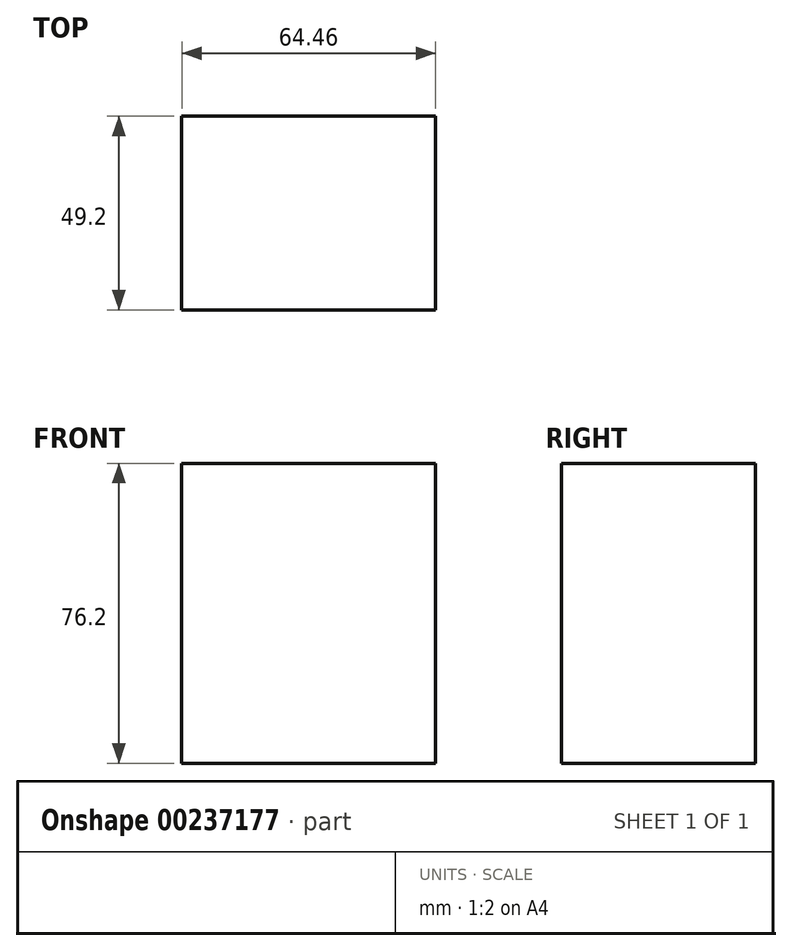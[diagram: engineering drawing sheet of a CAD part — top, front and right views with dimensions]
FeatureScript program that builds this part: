
annotation { "Feature Type Name" : "Feature", "Feature Type Description" : "" }
export const myFeature = defineFeature(function(context is Context, id is Id, definition is map)
    precondition{}
    {
        {
            var Q0;
            Q0=qCreatedBy(makeId("Top.planeOp"),FACE);
            var sketch = newSketch(context, id + "F0", { "sketchPlane" : qUnion([Q0])});
            skLineSegment(sketch, "E0.bottom", {"start": v(0, 0) * mm, "end": v(-64.46, 0) * mm});
            skLineSegment(sketch, "E0.top", {"start": v(0, 49.2) * mm, "end": v(-64.46, 49.2) * mm});
            skLineSegment(sketch, "E0.left", {"start": v(0, 0) * mm, "end": v(0, 49.2) * mm});
            skLineSegment(sketch, "E0.right", {"start": v(-64.46, 0) * mm, "end": v(-64.46, 49.2) * mm});
            skSolve(sketch);
        }
        {
            var Q0;
            Q0 = qSketchRegion(id + "F0", true);
            extrude(context, id + "F1", {"entities" : qUnion([Q0]), "depth" : 76.2 * mm});
        }
    });
